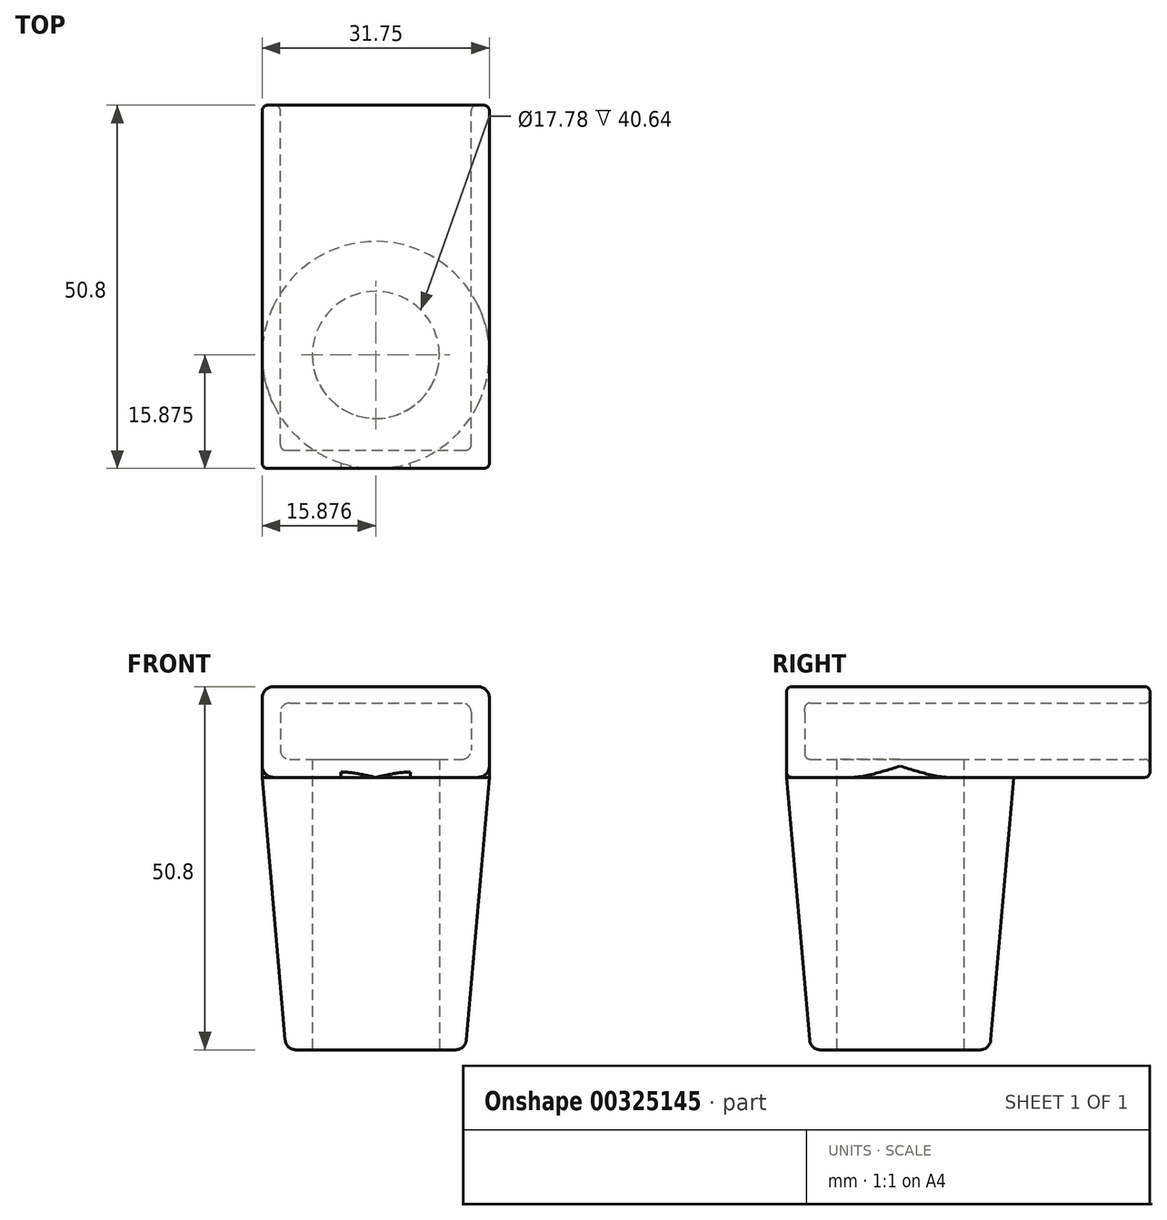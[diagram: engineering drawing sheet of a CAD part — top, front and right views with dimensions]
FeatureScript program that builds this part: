
annotation { "Feature Type Name" : "Feature", "Feature Type Description" : "" }
export const myFeature = defineFeature(function(context is Context, id is Id, definition is map)
    precondition{}
    {
        {
            var Q0;
            Q0=qCreatedBy(makeId("Front.planeOp"),FACE);
            var sketch = newSketch(context, id + "F0", { "sketchPlane" : qUnion([Q0])});
            skLineSegment(sketch, "E0.bottom", {"start": v(-0.65, 4.3) * mm, "end": v(27.92, 4.3) * mm});
            skLineSegment(sketch, "E0.top", {"start": v(-0.65, -8.4) * mm, "end": v(27.92, -8.4) * mm});
            skLineSegment(sketch, "E0.left", {"start": v(-2.24, 2.72) * mm, "end": v(-2.24, -6.8) * mm});
            skLineSegment(sketch, "E0.right", {"start": v(29.51, 2.72) * mm, "end": v(29.51, -6.8) * mm});
            skPoint(sketch, "E1.visualSharp", {"position": v(-2.24, 4.3) * mm});
            skArc(sketch, "E1.filletArc", {"start": v(-0.65, 4.3) * mm, "mid": v(-1.77, 3.84) * mm, "end": v(-2.24, 2.72) * mm});
            skPoint(sketch, "E2.visualSharp", {"position": v(29.51, 4.3) * mm});
            skArc(sketch, "E2.filletArc", {"start": v(29.51, 2.72) * mm, "mid": v(29.05, 3.84) * mm, "end": v(27.92, 4.3) * mm});
            skPoint(sketch, "E3.visualSharp", {"position": v(29.51, -8.4) * mm});
            skArc(sketch, "E3.filletArc", {"start": v(27.92, -8.4) * mm, "mid": v(29.05, -7.93) * mm, "end": v(29.51, -6.8) * mm});
            skPoint(sketch, "E4.visualSharp", {"position": v(-2.24, -8.4) * mm});
            skArc(sketch, "E4.filletArc", {"start": v(-2.24, -6.8) * mm, "mid": v(-1.77, -7.93) * mm, "end": v(-0.65, -8.4) * mm});
            skSolve(sketch);
        }
        {
            var Q0;
            Q0=makeQuery(id+"F0.imprint","IMPRINT",FACE,{"disambiguationData":[TD([[makeQuery(id+"F0.imprint","IMPRINT",EDGE,{"derivedFrom":sQuery(id+"F0.wireOp",EDGE,"E0.bottom")}),-1.0]])]});
            extrude(context, id + "F1", {"entities" : qUnion([Q0]), "depth" : 50.8 * mm});
        }
        {
            var Q0;
            Q0=makeQuery(id+"F1.opExtrude","SWEPT_FACE",FACE,{"disambiguationData":[OSD([sQuery(id+"F0.wireOp",EDGE,"E0.top")])]});
            var sketch = newSketch(context, id + "F2", { "sketchPlane" : qUnion([Q0])});
            skCircle(sketch, "E5", {"center": v(13.64, 34.93) * mm, "radius": 15.88 * mm});
            skSolve(sketch);
        }
        {
            var Q0;
            Q0 = qSketchRegion(id + "F2", true);
            extrude(context, id + "F3", {"entities" : qUnion([Q0]), "operationType" : NewBodyOperationType.ADD, "oppositeDirection" : true, "depth" : 5.08 * mm});
        }
        {
            var Q0;
            Q0 = qSketchRegion(id + "F2", true);
            extrude(context, id + "F4", {"entities" : qUnion([Q0]), "operationType" : NewBodyOperationType.ADD, "depth" : 38.1 * mm, "hasDraft" : true, "draftAngle" : 5 * degree, "draftPullDirection" : true});
        }
        {
            var Q0;
            Q0=makeQuery(id+"F4.opExtrude","CAP_FACE",FACE,{"disambiguationData":[OSD([sQuery(id+"F2.wireOp",EDGE,"E5")])],"isStart":false});
            var sketch = newSketch(context, id + "F5", { "sketchPlane" : qUnion([Q0])});
            skCircle(sketch, "E6.0", {"center": v(13.64, 34.93) * mm, "radius": 12.54 * mm});
            skCircle(sketch, "E7", {"center": v(13.64, 34.93) * mm, "radius": 8.9 * mm});
            skSolve(sketch);
        }
        {
            var Q0;
            Q0=makeQuery(id+"F5.imprint","IMPRINT",FACE,{"disambiguationData":[TD([[makeQuery(id+"F5.imprint","IMPRINT",EDGE,{"derivedFrom":sQuery(id+"F5.wireOp",EDGE,"E7")}),1.0]])]});
            extrude(context, id + "F6", {"entities" : qUnion([Q0]), "operationType" : NewBodyOperationType.REMOVE, "oppositeDirection" : true, "depth" : 40.64 * mm});
        }
        {
            var Q0;
            Q0=makeQuery(id+"F1.opExtrude","CAP_FACE",FACE,{"disambiguationData":[OSD([sQuery(id+"F0.wireOp",EDGE,"E0.bottom"),sQuery(id+"F0.wireOp",EDGE,"E0.top"),sQuery(id+"F0.wireOp",EDGE,"E0.left"),sQuery(id+"F0.wireOp",EDGE,"E0.right"),sQuery(id+"F0.wireOp",EDGE,"E1.filletArc"),sQuery(id+"F0.wireOp",EDGE,"E2.filletArc"),sQuery(id+"F0.wireOp",EDGE,"E3.filletArc"),sQuery(id+"F0.wireOp",EDGE,"E4.filletArc")])],"isStart":true});
            var sketch = newSketch(context, id + "F7", { "sketchPlane" : qUnion([Q0])});
            skLineSegment(sketch, "E8.0", {"start": v(-1.57, -5.85) * mm, "end": v(-25.7, -5.85) * mm});
            skLineSegment(sketch, "E9.0", {"start": v(-0.3, 0.73) * mm, "end": v(-0.3, -4.58) * mm});
            skLineSegment(sketch, "E10.0", {"start": v(0.65, 4.54) * mm, "end": v(-27.92, 4.54) * mm});
            skLineSegment(sketch, "E11.0", {"start": v(-1.57, 2) * mm, "end": v(-25.7, 2) * mm});
            skLineSegment(sketch, "E12.0", {"start": v(-26.97, 0.73) * mm, "end": v(-26.97, -4.58) * mm});
            skArc(sketch, "E13.filletArc", {"start": v(-26.97, -4.58) * mm, "mid": v(-26.6, -5.48) * mm, "end": v(-25.7, -5.85) * mm});
            skArc(sketch, "E14.filletArc", {"start": v(-25.7, 2) * mm, "mid": v(-26.6, 1.63) * mm, "end": v(-26.97, 0.73) * mm});
            skArc(sketch, "E15.filletArc", {"start": v(-0.3, 0.73) * mm, "mid": v(-0.67, 1.63) * mm, "end": v(-1.57, 2) * mm});
            skArc(sketch, "E16.filletArc", {"start": v(-1.57, -5.85) * mm, "mid": v(-0.67, -5.48) * mm, "end": v(-0.3, -4.58) * mm});
            skSolve(sketch);
        }
        {
            var Q0;
            Q0=makeQuery(id+"F7.imprint","IMPRINT",FACE,{"disambiguationData":[TD([[makeQuery(id+"F7.imprint","IMPRINT",EDGE,{"derivedFrom":sQuery(id+"F7.wireOp",EDGE,"E8.0")}),-1.0]])]});
            extrude(context, id + "F8", {"entities" : qUnion([Q0]), "operationType" : NewBodyOperationType.REMOVE, "oppositeDirection" : true, "depth" : 48.26 * mm});
        }
        {
            var Q0;
            Q0=makeQuery(id+"F4.opExtrude","CAP_EDGE",EDGE,{"disambiguationData":[OSD([sQuery(id+"F2.wireOp",EDGE,"E5")])],"isStart":false});
            var Q1;
            Q1=makeQuery(id+"F6.boolean.opBoolean","COPY",EDGE,{"derivedFrom":makeQuery(id+"F6.opExtrude","CAP_EDGE",EDGE,{"disambiguationData":[OSD([sQuery(id+"F5.wireOp",EDGE,"E7")])],"isStart":true})});
            fillet(context, id + "F9", {"entities" : qUnion([Q0, Q1]), "radius" : 1.52 * mm, "tangentPropagation" : true, "allowEdgeOverflow" : false});
        }
        {
            var Q0;
            Q0=makeQuery(id+"F1.opExtrude","CAP_EDGE",EDGE,{"disambiguationData":[OSD([sQuery(id+"F0.wireOp",EDGE,"E0.top")])],"isStart":true});
            var Q1;
            Q1=makeQuery(id+"F1.opExtrude","CAP_EDGE",EDGE,{"disambiguationData":[OSD([sQuery(id+"F0.wireOp",EDGE,"E3.filletArc")])],"isStart":true});
            var Q2;
            Q2=makeQuery(id+"F1.opExtrude","CAP_EDGE",EDGE,{"disambiguationData":[OSD([sQuery(id+"F0.wireOp",EDGE,"E0.right")])],"isStart":true});
            var Q3;
            Q3=makeQuery(id+"F1.opExtrude","CAP_EDGE",EDGE,{"disambiguationData":[OSD([sQuery(id+"F0.wireOp",EDGE,"E0.bottom")])],"isStart":true});
            var Q4;
            Q4=makeQuery(id+"F1.opExtrude","CAP_EDGE",EDGE,{"disambiguationData":[OSD([sQuery(id+"F0.wireOp",EDGE,"E1.filletArc")])],"isStart":true});
            var Q5;
            Q5=makeQuery(id+"F1.opExtrude","CAP_EDGE",EDGE,{"disambiguationData":[OSD([sQuery(id+"F0.wireOp",EDGE,"E4.filletArc")])],"isStart":true});
            var Q6;
            Q6=makeQuery(id+"F8.boolean.opBoolean","COPY",EDGE,{"derivedFrom":makeQuery(id+"F8.opExtrude","CAP_EDGE",EDGE,{"disambiguationData":[OSD([sQuery(id+"F7.wireOp",EDGE,"E8.0")])],"isStart":true})});
            var Q7;
            Q7=makeQuery(id+"F8.boolean.opBoolean","COPY",FACE,{"derivedFrom":makeQuery(id+"F8.opExtrude","SWEPT_FACE",FACE,{"disambiguationData":[OSD([sQuery(id+"F7.wireOp",EDGE,"E11.0")])]})});
            fillet(context, id + "F10", {"entities" : qUnion([Q0, Q1, Q2, Q3, Q4, Q5, Q6, Q7]), "radius" : 0.76 * mm, "tangentPropagation" : true, "allowEdgeOverflow" : false});
        }
        {
            var Q0;
            Q0=makeQuery(id+"F1.opExtrude","CAP_EDGE",EDGE,{"disambiguationData":[OSD([sQuery(id+"F0.wireOp",EDGE,"E0.right")])],"isStart":false});
            var Q1;
            Q1=makeQuery(id+"F1.opExtrude","CAP_EDGE",EDGE,{"disambiguationData":[OSD([sQuery(id+"F0.wireOp",EDGE,"E3.filletArc")])],"isStart":false});
            fillet(context, id + "F11", {"entities" : qUnion([Q0, Q1]), "radius" : 0.76 * mm, "tangentPropagation" : true, "allowEdgeOverflow" : false});
        }
    });
